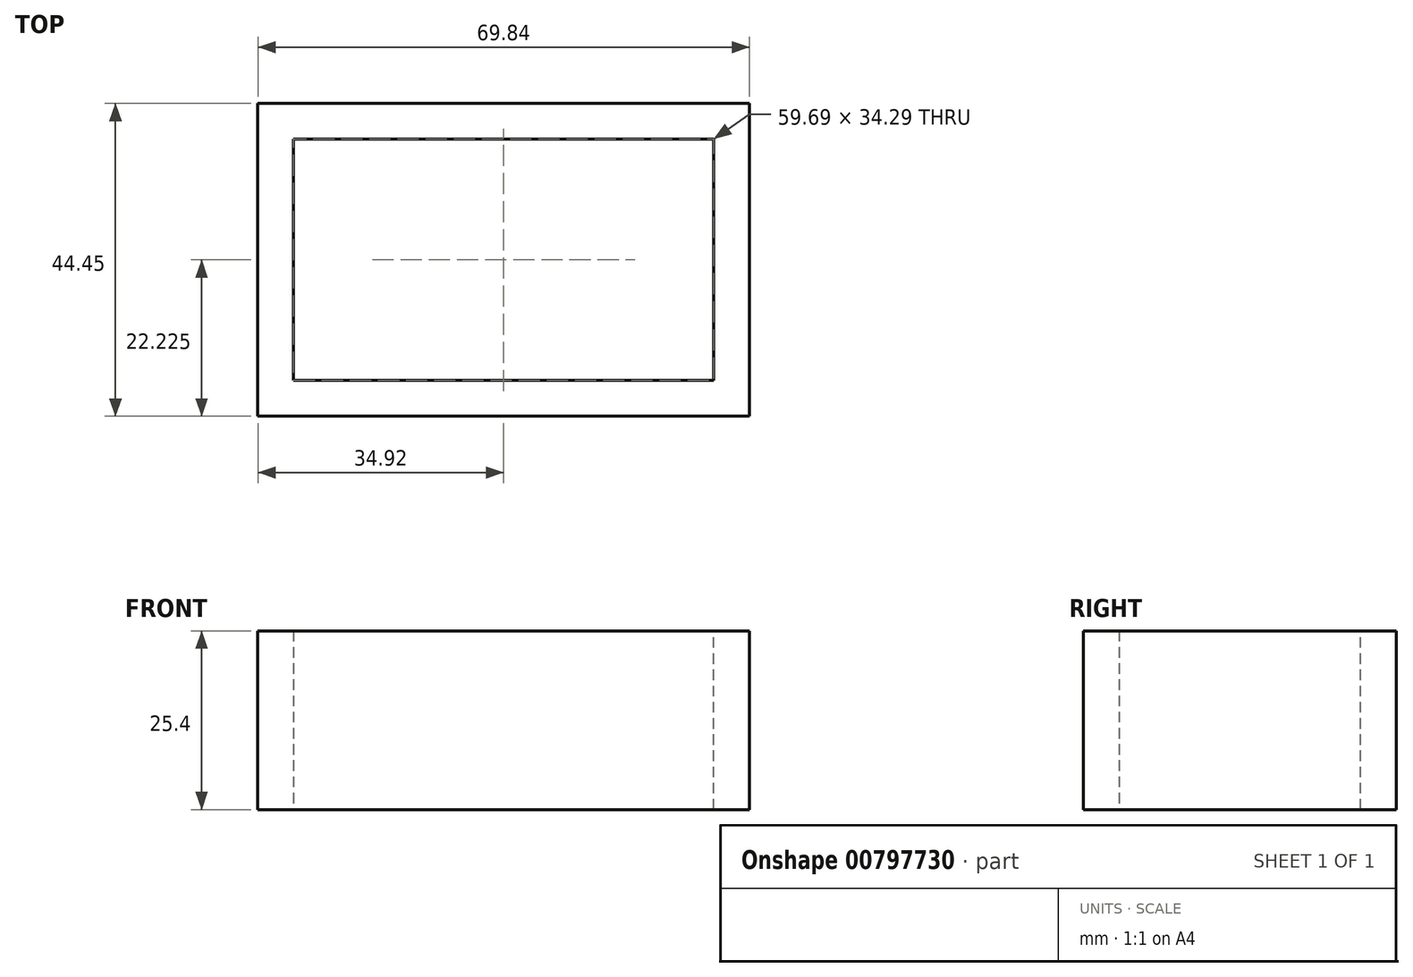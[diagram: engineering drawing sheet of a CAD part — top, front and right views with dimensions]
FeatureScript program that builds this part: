
annotation { "Feature Type Name" : "Feature", "Feature Type Description" : "" }
export const myFeature = defineFeature(function(context is Context, id is Id, definition is map)
    precondition{}
    {
        {
            var Q0;
            Q0=qCreatedBy(makeId("Front.planeOp"),FACE);
            var sketch = newSketch(context, id + "F0", { "sketchPlane" : qUnion([Q0])});
            skLineSegment(sketch, "E0.bottom", {"start": v(-34.92, 12.7) * mm, "end": v(34.93, 12.7) * mm});
            skLineSegment(sketch, "E0.top", {"start": v(-34.93, -12.7) * mm, "end": v(34.92, -12.7) * mm});
            skLineSegment(sketch, "E0.left", {"start": v(-34.93, 12.7) * mm, "end": v(-34.93, -12.7) * mm});
            skLineSegment(sketch, "E0.right", {"start": v(34.93, 12.7) * mm, "end": v(34.93, -12.7) * mm});
            skPoint(sketch, "E0.middle", {"position": v(0, 0) * mm});
            skSolve(sketch);
        }
        {
            var Q0;
            Q0=makeQuery(id+"F0.imprint","IMPRINT",FACE,{"disambiguationData":[TD([[makeQuery(id+"F0.imprint","IMPRINT",EDGE,{"derivedFrom":sQuery(id+"F0.wireOp",EDGE,"E0.bottom")}),-1.0]])]});
            extrude(context, id + "F1", {"entities" : qUnion([Q0]), "depth" : 5.08 * mm, "offsetDistance" : 25.4 * mm});
        }
        {
            var Q0;
            Q0=makeQuery(id+"F1.opExtrude","SWEPT_FACE",FACE,{"disambiguationData":[OSD([sQuery(id+"F0.wireOp",EDGE,"E0.left")])]});
            var sketch = newSketch(context, id + "F2", { "sketchPlane" : qUnion([Q0])});
            skLineSegment(sketch, "E1.bottom", {"start": v(0, 12.7) * mm, "end": v(44.45, 12.7) * mm});
            skLineSegment(sketch, "E1.top", {"start": v(0, -12.7) * mm, "end": v(44.45, -12.7) * mm});
            skLineSegment(sketch, "E1.left", {"start": v(0, 12.7) * mm, "end": v(0, -12.7) * mm});
            skLineSegment(sketch, "E1.right", {"start": v(44.45, 12.7) * mm, "end": v(44.45, -12.7) * mm});
            skSolve(sketch);
        }
        {
            var Q0;
            {var subQ2=sQuery(id+"F2.wireOp",EDGE,"E1.right");Q0=makeQuery(id+"F2.imprint","IMPRINT",FACE,{"disambiguationData":[TD([[makeQuery(id+"F2.imprint","IMPRINT",EDGE,{"derivedFrom":subQ2}),-1.0]])]});}
            extrude(context, id + "F3", {"entities" : qUnion([Q0]), "operationType" : NewBodyOperationType.ADD, "oppositeDirection" : true, "depth" : 5.08 * mm, "offsetDistance" : 25.4 * mm});
        }
        {
            var Q0;
            Q0=makeQuery(id+"F3.opExtrude","SWEPT_FACE",FACE,{"disambiguationData":[OSD([sQuery(id+"F2.wireOp",EDGE,"E1.right")])]});
            var sketch = newSketch(context, id + "F4", { "sketchPlane" : qUnion([Q0])});
            skLineSegment(sketch, "E2.bottom", {"start": v(-34.93, 12.7) * mm, "end": v(34.92, 12.7) * mm});
            skLineSegment(sketch, "E2.top", {"start": v(-34.93, -12.7) * mm, "end": v(34.93, -12.7) * mm});
            skLineSegment(sketch, "E2.left", {"start": v(-34.93, 12.7) * mm, "end": v(-34.93, -12.7) * mm});
            skLineSegment(sketch, "E2.right", {"start": v(34.92, 12.7) * mm, "end": v(34.92, -12.7) * mm});
            skSolve(sketch);
        }
        {
            var Q0;
            {var subQ2=sQuery(id+"F4.wireOp",EDGE,"E2.right");Q0=makeQuery(id+"F4.imprint","IMPRINT",FACE,{"disambiguationData":[TD([[makeQuery(id+"F4.imprint","IMPRINT",EDGE,{"derivedFrom":subQ2}),-1.0]])]});}
            extrude(context, id + "F5", {"entities" : qUnion([Q0]), "operationType" : NewBodyOperationType.ADD, "oppositeDirection" : true, "depth" : 5.08 * mm, "offsetDistance" : 25.4 * mm});
        }
        {
            var Q0;
            Q0=makeQuery(id+"F5.opExtrude","SWEPT_FACE",FACE,{"disambiguationData":[OSD([sQuery(id+"F4.wireOp",EDGE,"E2.right")])]});
            var sketch = newSketch(context, id + "F6", { "sketchPlane" : qUnion([Q0])});
            skLineSegment(sketch, "E3.bottom", {"start": v(-44.45, 12.7) * mm, "end": v(0, 12.7) * mm});
            skLineSegment(sketch, "E3.top", {"start": v(-44.45, -12.7) * mm, "end": v(0, -12.7) * mm});
            skLineSegment(sketch, "E3.left", {"start": v(-44.45, 12.7) * mm, "end": v(-44.45, -12.7) * mm});
            skLineSegment(sketch, "E3.right", {"start": v(0, 12.7) * mm, "end": v(0, -12.7) * mm});
            skSolve(sketch);
        }
        {
            var Q0;
            {var subQ2=sQuery(id+"F6.wireOp",EDGE,"E3.right");Q0=makeQuery(id+"F6.imprint","IMPRINT",FACE,{"disambiguationData":[TD([[makeQuery(id+"F6.imprint","IMPRINT",EDGE,{"derivedFrom":subQ2}),-1.0]])]});}
            extrude(context, id + "F7", {"entities" : qUnion([Q0]), "operationType" : NewBodyOperationType.ADD, "oppositeDirection" : true, "depth" : 5.08 * mm, "offsetDistance" : 25.4 * mm});
        }
    });
